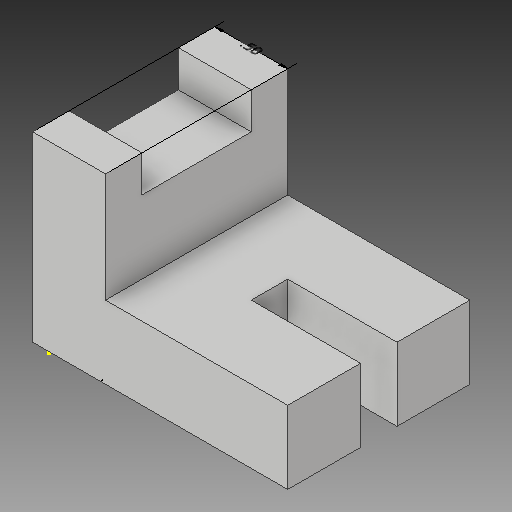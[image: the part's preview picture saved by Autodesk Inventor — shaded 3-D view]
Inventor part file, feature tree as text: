
AUTODESK INVENTOR PART (.ipt)
format: ipt  version: 2018 (Build 220112000, 112)  size: 139,264 bytes
history: native  units: in
note: dims shown in document units (in); Inventor stores cm internally (conversion verified against a paired STEP export)
features: sketch x4, other x3, extrude x3
ambient origin geometry x8: Origin, YZ Plane, XZ Plane, XY Plane, X Axis, Y Axis, Z Axis, Center Point
bodies: Solid1 (feature_tree)
feature tree (10):
  other  "Annotations"
  extrude  "Extrusion1"  Depth=1.25in
  extrude  "Extrusion2"  Depth=0.5in
  extrude  "Extrusion3"  Depth=1.25in TaperAngle=0.0deg
  sketch  "Sketch4"  dims[d11=0.625in d13=0.25in d14=0.125in d15=0.75in d16=0.0in d17=1.75in d18=0.25in d19=0.25in d20=0.25in d21=0.75in d22=0.0in d23=0.1064in d24=0.0031in d25=1.25in d26=0.0in d27=0.3937in d28=0.5in]
  sketch  "Sketch1"  dims[d0=0.5in d1=1.25in]
  sketch  "Sketch2"  dims[d4=1.25in d5=0.5in]
  sketch  "Sketch3"  dims[d6=0.5in d7=1.25in d8=0.0in]
  other  "Linear Dimension 1"
  other  "Linear Dimension 2"
